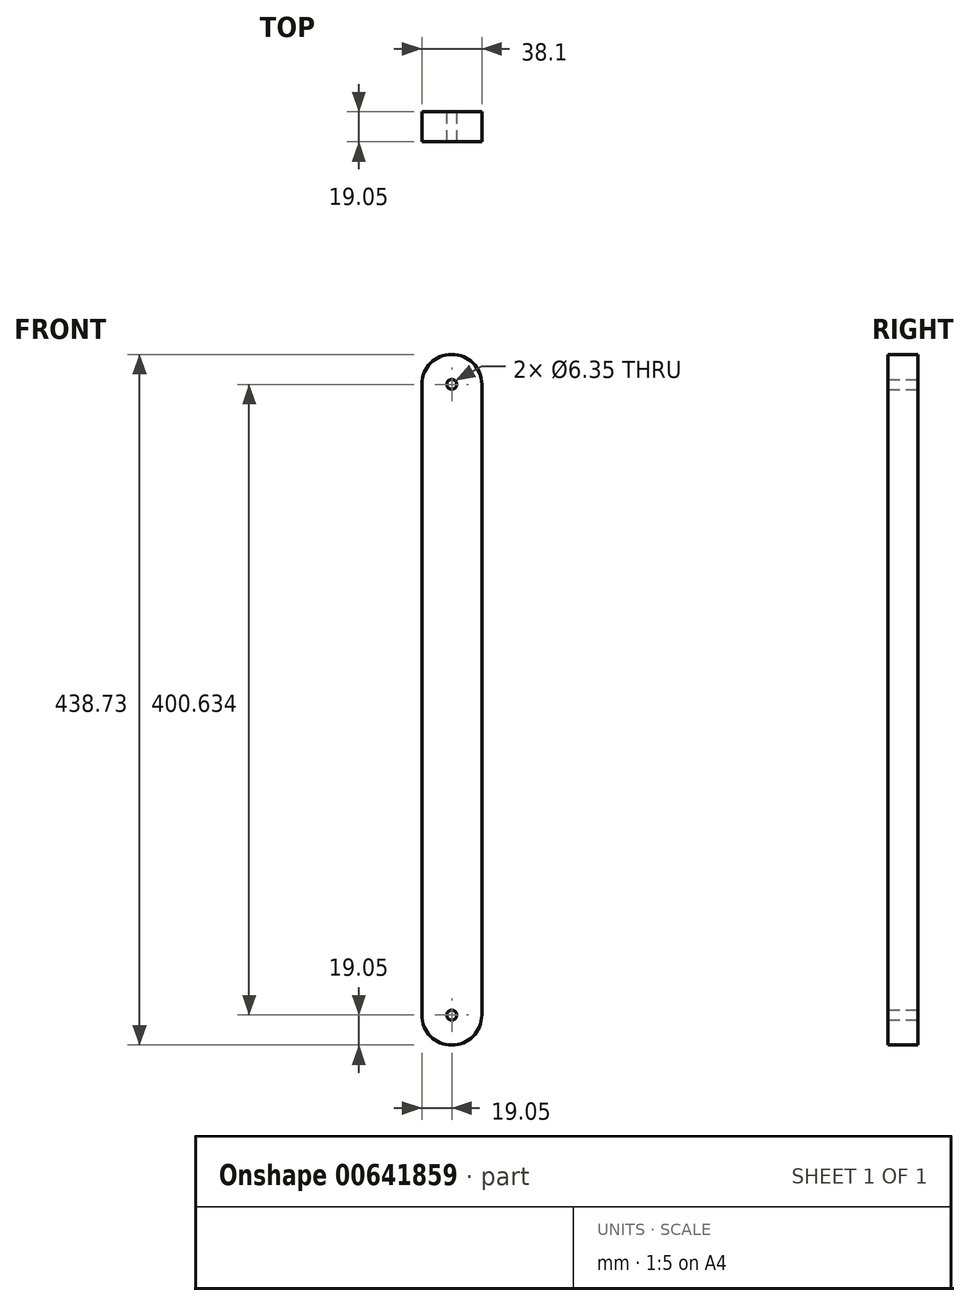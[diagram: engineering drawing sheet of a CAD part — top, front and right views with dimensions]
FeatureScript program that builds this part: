
annotation { "Feature Type Name" : "Feature", "Feature Type Description" : "" }
export const myFeature = defineFeature(function(context is Context, id is Id, definition is map)
    precondition{}
    {
        {
            var Q0;
            Q0=qCreatedBy(makeId("Front.planeOp"),FACE);
            var sketch = newSketch(context, id + "F0", { "sketchPlane" : qUnion([Q0])});
            skLineSegment(sketch, "E0.bottom", {"start": v(0, 0) * mm, "end": v(38.1, 0) * mm, "construction": true});
            skLineSegment(sketch, "E0.top", {"start": v(0, 400.63) * mm, "end": v(38.1, 400.63) * mm, "construction": true});
            skLineSegment(sketch, "E0.left", {"start": v(0, 0) * mm, "end": v(0, 400.63) * mm});
            skLineSegment(sketch, "E0.right", {"start": v(38.1, 0) * mm, "end": v(38.1, 400.63) * mm});
            skArc(sketch, "E1", {"start": v(38.1, 400.63) * mm, "mid": v(19.05, 419.68) * mm, "end": v(0, 400.63) * mm});
            skPoint(sketch, "E2.center.orphan", {"position": v(19.05, 0) * mm});
            skCircle(sketch, "E3", {"center": v(19.05, 0) * mm, "radius": 19.05 * mm, "construction": true});
            skCircle(sketch, "E4", {"center": v(19.05, 400.63) * mm, "radius": 3.18 * mm});
            skCircle(sketch, "E5", {"center": v(19.05, 0) * mm, "radius": 3.18 * mm});
            skArc(sketch, "E6", {"start": v(0, 0) * mm, "mid": v(19.05, -19.05) * mm, "end": v(38.1, 0) * mm});
            skSolve(sketch);
        }
        {
            var Q0;
            Q0=makeQuery(id+"F0.imprint","IMPRINT",FACE,{"disambiguationData":[TD([[makeQuery(id+"F0.imprint","IMPRINT",EDGE,{"derivedFrom":sQuery(id+"F0.wireOp",EDGE,"E0.left")}),-1.0]])]});
            var Q1;
            Q1 = qBodyType(qCreatedBy(id + "F0" ,EDGE), BodyType.WIRE);
            extrude(context, id + "F1", {"entities" : qUnion([Q0]), "surfaceEntities" : qUnion([Q1]), "depth" : 19.05 * mm, "offsetDistance" : 25.4 * mm});
        }
    });
